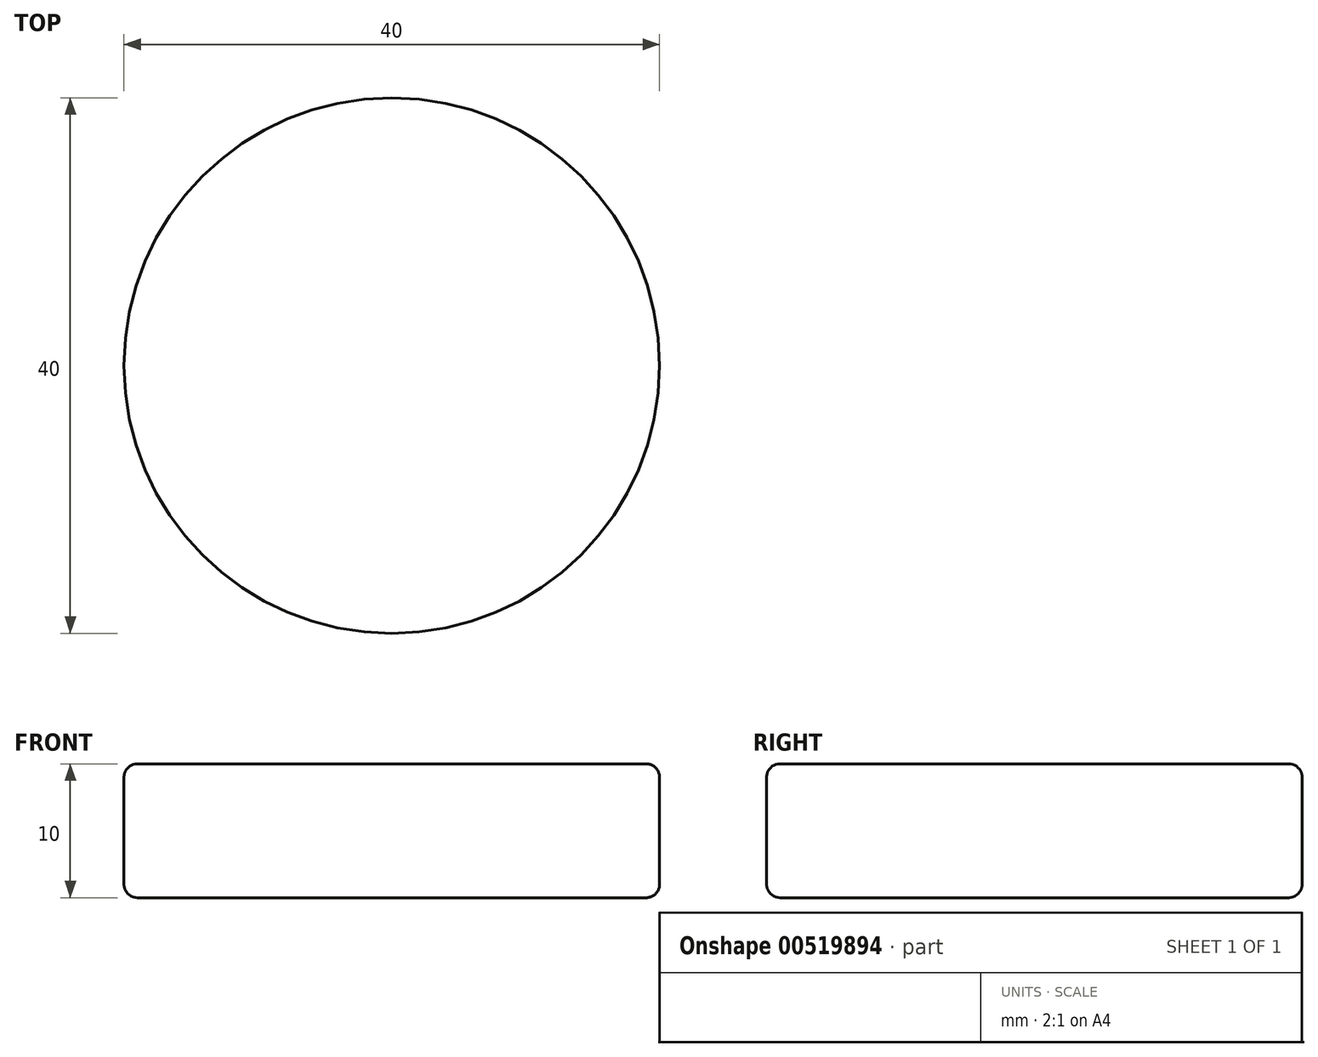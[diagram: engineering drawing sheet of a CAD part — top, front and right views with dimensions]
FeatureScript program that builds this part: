
annotation { "Feature Type Name" : "Feature", "Feature Type Description" : "" }
export const myFeature = defineFeature(function(context is Context, id is Id, definition is map)
    precondition{}
    {
        {
            var Q0;
            Q0=qCreatedBy(makeId("Top.planeOp"),FACE);
            var sketch = newSketch(context, id + "F0", { "sketchPlane" : qUnion([Q0])});
            skCircle(sketch, "E0", {"center": v(0, 0) * mm, "radius": 20 * mm});
            skCircle(sketch, "E1", {"center": v(0, 0) * mm, "radius": 25 * mm});
            skSolve(sketch);
        }
        {
            var Q0;
            Q0=makeQuery(id+"F0.imprint","IMPRINT",FACE,{"disambiguationData":[TD([[makeQuery(id+"F0.imprint","IMPRINT",EDGE,{"derivedFrom":sQuery(id+"F0.wireOp",EDGE,"E0")}),1.0]])]});
            extrude(context, id + "F1", {"entities" : qUnion([Q0]), "depth" : 10 * mm, "offsetDistance" : 25 * mm});
        }
        {
            var Q0;
            Q0=makeQuery(id+"F1.opExtrude","CAP_FACE",FACE,{"disambiguationData":[OSD([sQuery(id+"F0.wireOp",EDGE,"E0")])],"isStart":false});
            var sketch = newSketch(context, id + "F2", { "sketchPlane" : qUnion([Q0])});
            skCircle(sketch, "E2", {"center": v(0, 0) * mm, "radius": 25 * mm});
            skSolve(sketch);
        }
        {
            var Q0;
            Q0=makeQuery(id+"F1.opExtrude","CAP_EDGE",EDGE,{"disambiguationData":[OSD([sQuery(id+"F0.wireOp",EDGE,"E0")])],"isStart":true});
            fillet(context, id + "F3", {"entities" : qUnion([Q0]), "radius" : 1 * mm, "tangentPropagation" : true, "allowEdgeOverflow" : false});
        }
        {
            var Q0;
            Q0=makeQuery(id+"F1.opExtrude","CAP_EDGE",EDGE,{"disambiguationData":[OSD([sQuery(id+"F0.wireOp",EDGE,"E0")])],"isStart":false});
            fillet(context, id + "F4", {"entities" : qUnion([Q0]), "radius" : 1 * mm, "tangentPropagation" : true, "allowEdgeOverflow" : false});
        }
        {
            var Q0;
            Q0=sQuery(id+"F2.wireOp",EDGE,"E2");
            extrude(context, id + "F5", {"bodyType" : ToolBodyType.SURFACE, "surfaceEntities" : qUnion([Q0]), "depth" : 2 * mm, "offsetDistance" : 25 * mm});
        }
    });
